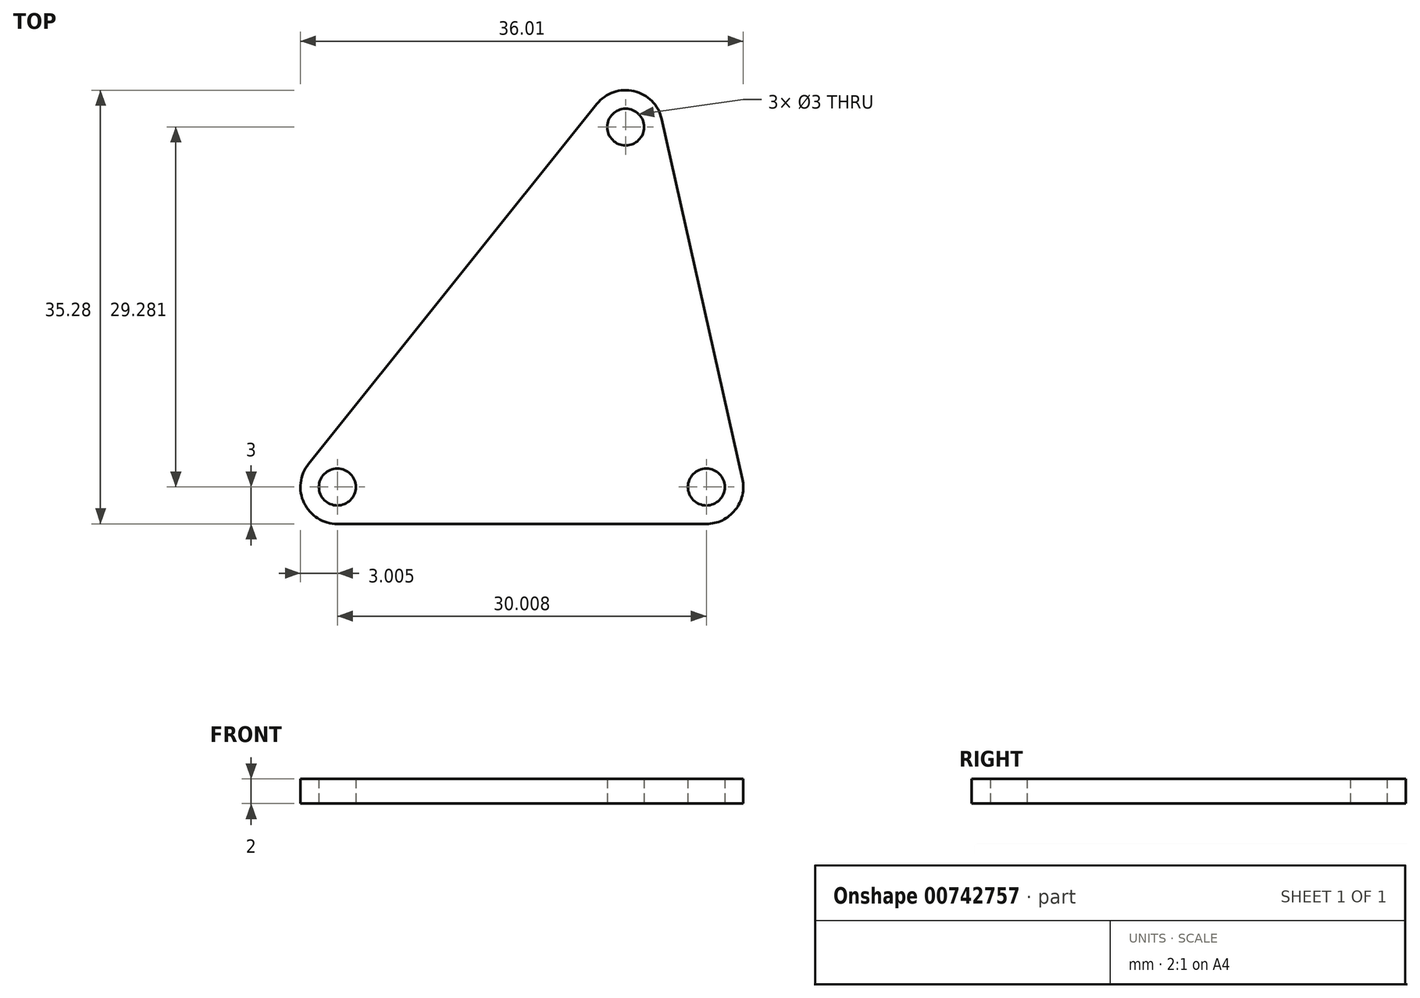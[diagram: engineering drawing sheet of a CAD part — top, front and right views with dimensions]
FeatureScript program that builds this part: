
annotation { "Feature Type Name" : "Feature", "Feature Type Description" : "" }
export const myFeature = defineFeature(function(context is Context, id is Id, definition is map)
    precondition{}
    {
        {
            var Q0;
            Q0=qCreatedBy(makeId("Top.planeOp"),FACE);
            var sketch = newSketch(context, id + "F0", { "sketchPlane" : qUnion([Q0])});
            skLineSegment(sketch, "E0", {"start": v(-0.82, 3.66) * mm, "end": v(-7.38, 32.94) * mm});
            skLineSegment(sketch, "E1", {"start": v(-12.65, 34.16) * mm, "end": v(-36.1, 4.87) * mm});
            skLineSegment(sketch, "E2", {"start": v(-33.76, 0) * mm, "end": v(-3.75, 0) * mm});
            skLineSegment(sketch, "E3.0", {"start": v(-10.31, 32.28) * mm, "end": v(-33.76, 3) * mm, "construction": true});
            skLineSegment(sketch, "E3.1", {"start": v(-3.75, 3) * mm, "end": v(-10.31, 32.28) * mm, "construction": true});
            skLineSegment(sketch, "E3.2", {"start": v(-33.76, 3) * mm, "end": v(-3.75, 3) * mm, "construction": true});
            skPoint(sketch, "E4.visualSharp", {"position": v(-8.75, 39.03) * mm});
            skArc(sketch, "E4.filletArc", {"start": v(-7.38, 32.94) * mm, "mid": v(-9.64, 35.2) * mm, "end": v(-12.65, 34.16) * mm});
            skPoint(sketch, "E5.visualSharp", {"position": v(0, 0) * mm});
            skArc(sketch, "E5.filletArc", {"start": v(-3.75, 0) * mm, "mid": v(-1.4, 1.13) * mm, "end": v(-0.82, 3.66) * mm});
            skPoint(sketch, "E6.visualSharp", {"position": v(-40, 0) * mm});
            skArc(sketch, "E6.filletArc", {"start": v(-36.1, 4.87) * mm, "mid": v(-36.46, 1.7) * mm, "end": v(-33.76, 0) * mm});
            skCircle(sketch, "E7", {"center": v(-10.31, 32.28) * mm, "radius": 1.5 * mm});
            skCircle(sketch, "E8", {"center": v(-3.75, 3) * mm, "radius": 1.5 * mm});
            skCircle(sketch, "E9", {"center": v(-33.76, 3) * mm, "radius": 1.5 * mm});
            skSolve(sketch);
        }
        {
            var Q0;
            Q0 = qSketchRegion(id + "F0", true);
            extrude(context, id + "F1", {"entities" : qUnion([Q0]), "depth" : 2 * mm, "offsetDistance" : 25 * mm});
        }
    });
